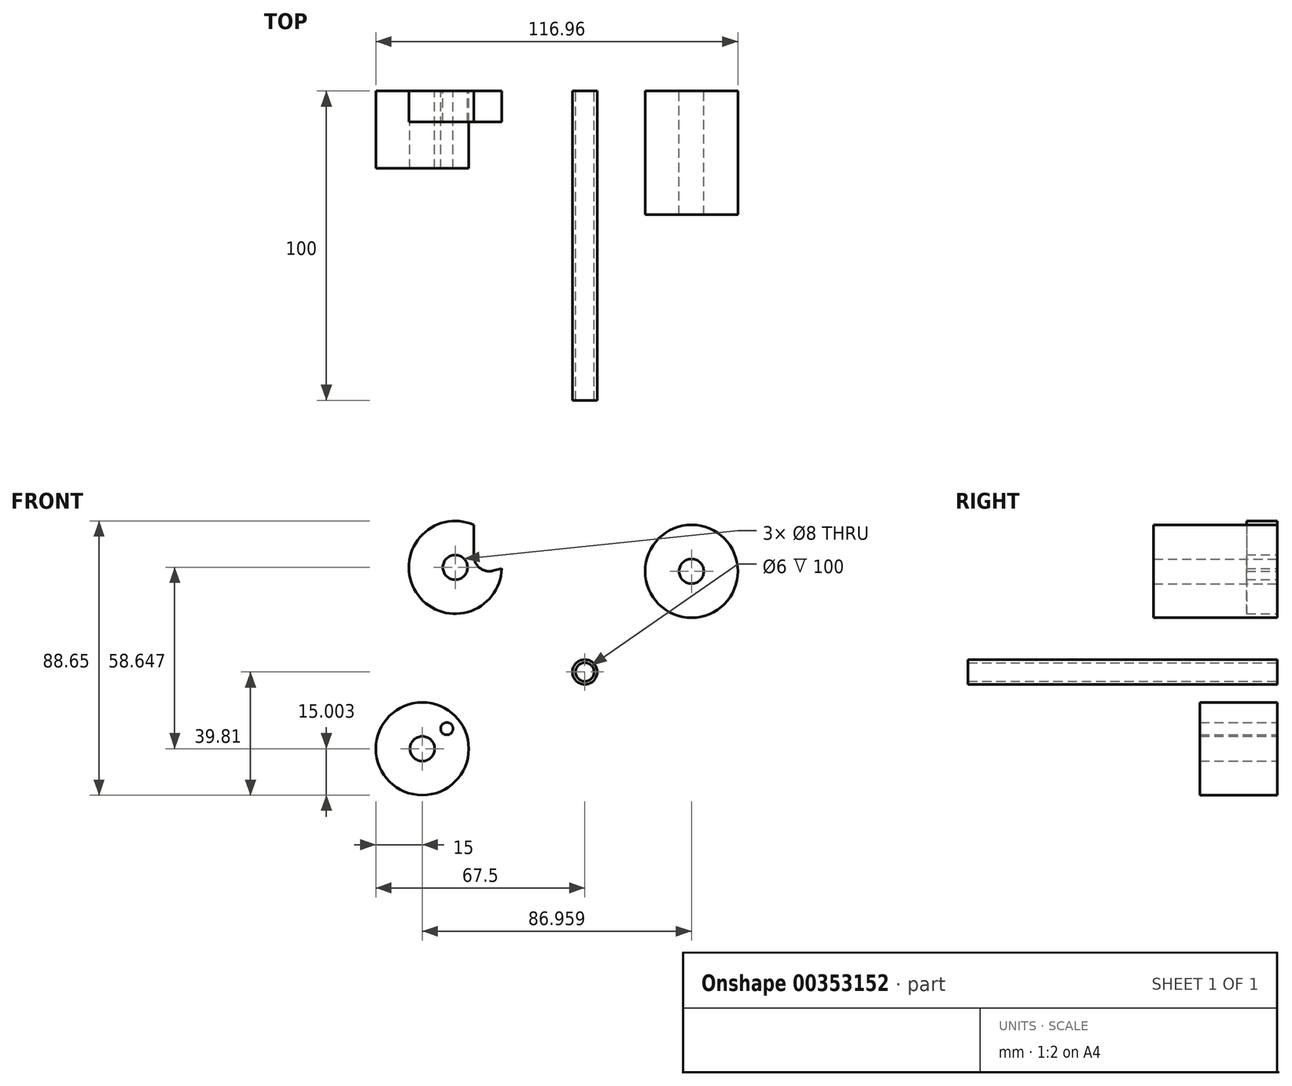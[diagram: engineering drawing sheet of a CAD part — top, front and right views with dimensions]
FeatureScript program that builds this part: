
annotation { "Feature Type Name" : "Feature", "Feature Type Description" : "" }
export const myFeature = defineFeature(function(context is Context, id is Id, definition is map)
    precondition{}
    {
        {
            var Q0;
            Q0=qCreatedBy(makeId("Front.planeOp"),FACE);
            var sketch = newSketch(context, id + "F0", { "sketchPlane" : qUnion([Q0])});
            skCircle(sketch, "E0", {"center": v(0, 0) * mm, "radius": 4 * mm});
            skCircle(sketch, "E1", {"center": v(0, 0) * mm, "radius": 3 * mm});
            skSolve(sketch);
        }
        {
            var Q0;
            Q0 = qSketchRegion(id + "F0", true);
            extrude(context, id + "F1", {"entities" : qUnion([Q0]), "depth" : 100 * mm});
        }
        {
            var Q0;
            Q0=qCreatedBy(makeId("Front.planeOp"),FACE);
            var sketch = newSketch(context, id + "F2", { "sketchPlane" : qUnion([Q0])});
            skCircle(sketch, "E2", {"center": v(34.46, 32.56) * mm, "radius": 15 * mm});
            skCircle(sketch, "E3", {"center": v(34.46, 32.56) * mm, "radius": 4 * mm});
            skSolve(sketch);
        }
        {
            var Q0;
            Q0=makeQuery(id+"F2.imprint","IMPRINT",FACE,{"disambiguationData":[TD([[makeQuery(id+"F2.imprint","IMPRINT",EDGE,{"derivedFrom":sQuery(id+"F2.wireOp",EDGE,"E2")}),1.0]])]});
            extrude(context, id + "F3", {"entities" : qUnion([Q0]), "depth" : 40 * mm});
        }
        {
            var Q0;
            Q0=qCreatedBy(makeId("Front.planeOp"),FACE);
            var sketch = newSketch(context, id + "F4", { "sketchPlane" : qUnion([Q0])});
            skArc(sketch, "E4", {"start": v(-35.83, 47.57) * mm, "mid": v(-54.53, 25.79) * mm, "end": v(-26.88, 33.5) * mm});
            skCircle(sketch, "E5", {"center": v(-41.87, 33.84) * mm, "radius": 4 * mm});
            skLineSegment(sketch, "E6", {"start": v(-35.83, 47.57) * mm, "end": v(-35.83, 37.57) * mm});
            skLineSegment(sketch, "E7", {"start": v(-29.46, 32.76) * mm, "end": v(-26.88, 33.5) * mm});
            skPoint(sketch, "E8.visualSharp", {"position": v(-35.83, 30.94) * mm});
            skArc(sketch, "E8.filletArc", {"start": v(-35.83, 37.57) * mm, "mid": v(-33.84, 33.58) * mm, "end": v(-29.46, 32.76) * mm});
            skSolve(sketch);
        }
        {
            var Q0;
            Q0 = qSketchRegion(id + "F4", true);
            extrude(context, id + "F5", {"entities" : qUnion([Q0]), "depth" : 10 * mm});
        }
        {
            var Q0;
            Q0=qCreatedBy(makeId("Front.planeOp"),FACE);
            var sketch = newSketch(context, id + "F6", { "sketchPlane" : qUnion([Q0])});
            skCircle(sketch, "E9", {"center": v(-52.5, -24.8) * mm, "radius": 15 * mm});
            skCircle(sketch, "E10", {"center": v(-52.5, -24.8) * mm, "radius": 4 * mm});
            skCircle(sketch, "E11", {"center": v(-44.56, -18.31) * mm, "radius": 2 * mm});
            skSolve(sketch);
        }
        {
            var Q0;
            Q0=makeQuery(id+"F6.imprint","IMPRINT",FACE,{"disambiguationData":[TD([[makeQuery(id+"F6.imprint","IMPRINT",EDGE,{"derivedFrom":sQuery(id+"F6.wireOp",EDGE,"E9")}),1.0]])]});
            extrude(context, id + "F7", {"entities" : qUnion([Q0]), "depth" : 25 * mm});
        }
    });
